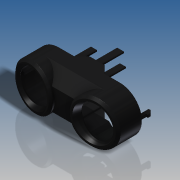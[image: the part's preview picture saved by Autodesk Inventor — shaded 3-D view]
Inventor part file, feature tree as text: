
AUTODESK INVENTOR PART (.ipt)
format: ipt  version: 2016 SP2 (Build 200236200, 236)  size: 1,308,672 bytes
history: native  units: in
note: dims shown in document units (in); Inventor stores cm internally (conversion verified against a paired STEP export)
features: sketch x19, extrude x17, other x8, plane x7, loft x6, projected_geometry x5, mirror x1, fillet x1
ambient origin geometry x8: Origin, YZ Plane, XZ Plane, XY Plane, X Axis, Y Axis, Z Axis, Center Point
bodies: Solid3 (feature_tree)
feature tree (64):
  sketch  "Sketch2"  dims[d4=0.1575in d5=0.315in]
  extrude  "Extrusion23"  Depth=0.315in
  plane  "Work Plane2"
  sketch  "Sketch11"  dims[d39=0.0457in d65=0.126in]
  extrude  "Extrusion24"  Depth=0.0467in
  sketch  "Sketch12"  dims[d66=0.0315in d69=0.4724in]
  plane  "Work Plane4"
  sketch  "Sketch15"  dims[d90=0.0598in d92=0.0315in]
  loft  "Loft1"
  loft  "Loft3"
  loft  "Loft4"
  plane  "Work Plane3"
  sketch  "Sketch14"  dims[d88=0.0441in d89=0.0504in]
  extrude  "Extrusion26"  Depth=0.063in
  sketch  "Sketch16"  dims[d109=0.9449in d111=0.0472in]
  extrude  "Extrusion27"  Depth=0.0504in
  extrude  "Extrusion28"  Depth=0.0315in
  extrude  "Extrusion29"  Depth=0.0472in
  sketch  "Sketch17"  dims[d113=0.063in d116=0.1417in]
  sketch  "Sketch18"  dims[d117=0.4867in d119=1.1156in]
  sketch  "Sketch21"  dims[d126=0.9134in d127=0.0in d128=0.9134in d129=0.0in]
  plane  "Work Plane5"
  loft  "Loft6"
  mirror  "Mirror4"
  sketch  "Sketch4"  dims[d6=0.6299in d9=0.0467in]
  extrude  "Extrusion30"  Depth=1.1156in
  plane  "Work Plane6"
  sketch  "Sketch22"  dims[d130=0.822in d131=0.7398in]
  plane  "Work Plane7"
  loft  "Loft7"
  sketch  "Sketch24"  dims[d134=0.9134in d135=0.0in d136=0.9134in d137=0.0in]
  plane  "Work Plane8"
  sketch  "Sketch26"  dims[d148=0.9134in d149=0.0in d150=0.5417in d151=0.2283in d152=0.0394in d153=0.2504in d154=0.2425in d155=0.0472in d156=0.4567in d157=0.9096in d158=0.9605in d159=0.378in d160=0.0378in d161=0.0274in d164=0.9134in d165=0.0in d166=-0.4646in d167=0.0in d168=90.0deg d169=0.0in d170=90.0deg d171=0.0in d172=90.0deg d173=0.0in d174=90.0deg d175=0.9134in d176=0.0in d177=0.9134in d178=0.0in d179=0.9134in d180=0.0in d184=0.0344in d185=60.0deg d196=0.0in d197=90.0deg d198=0.0in d199=90.0deg d200=0.0in d201=90.0deg d202=0.0in d203=90.0deg d204=0.7874in d205=0.0in d206=90.0deg d207=0.0in d208=90.0deg d210=0.1575in d211=0.9134in d212=0.0in d213=0.0in d214=90.0deg d215=0.0in d216=90.0deg d217=0.8189in d220=0.3937in d221=0.0in d222=0.0315in d223=0.6457in d224=0.2992in d225=0.0in d226=0.0in d227=0.3937in d228=0.2992in d229=0.0in d230=0.0in d231=0.5669in d232=0.378in d233=0.0in d234=0.0in d235=0.378in d236=0.252in d237=0.063in d238=0.0in d239=0.0039in d240=0.8189in d241=0.0472in d242=0.8189in d243=0.0in d244=90.0deg d245=0.0in d246=90.0deg d247=0.0in d248=90.0deg d249=0.0in d250=90.0deg]
  loft  "Loft8"
  extrude  "Extrusion32"  Depth=0.9134in TaperAngle=0.0deg
  sketch  "Sketch8"  dims[d30=0.315in d32=0.6299in]
  extrude  "Extrusion33"  Depth=0.7398in
  extrude  "Extrusion34"  [1 undecoded]
  extrude  "Extrusion35"  Depth=0.9134in TaperAngle=0.0deg
  extrude  "Extrusion36"  TaperAngle=0.0deg  [1 undecoded]
  fillet  "Fillet3"  [1 undecoded]
  other  "Srf2"
  other  "Srf3"
  other  "Srf4"
  other  "Srf5"
  other  "Srf6"
  sketch  "Sketch13"  dims[d70=0.189in d87=0.063in]
  sketch  "Sketch19"  dims[d120=2.1732in d121=0.6553in]
  sketch  "Sketch20"  dims[d122=0.9134in d123=0.0in d125=0.8119in]
  other  "Edges1"
  sketch  "Sketch23"  dims[d132=0.6614in d133=-0.3883in]
  projected_geometry  "Projected Loop1"
  sketch  "Sketch25"  dims[d138=0.9134in d139=0.0in d140=0.0in d141=90.0deg d142=0.0in d143=90.0deg]
  other  "Edges2"
  other  "Edges3"
  extrude  "ExtrusionSrf1"  Depth=0.9134in TaperAngle=0.0deg
  extrude  "ExtrusionSrf2"  [1 undecoded]
  extrude  "ExtrusionSrf3"  TaperAngle=0.0deg  [1 undecoded]
  extrude  "ExtrusionSrf4"  TaperAngle=0.0deg  [1 undecoded]
  extrude  "ExtrusionSrf5"  TaperAngle=0.0deg  [1 undecoded]
  projected_geometry  "Project Cut Edges1"
  projected_geometry  "Project Cut Edges2"
  projected_geometry  "Project Cut Edges3"
  projected_geometry  "Project Cut Edges4"
note: 7 required parameter values undecoded (feature->parameter linkage not recoverable at this tier; creation-order binding heuristic only, values carry confidence <= 0.55)
